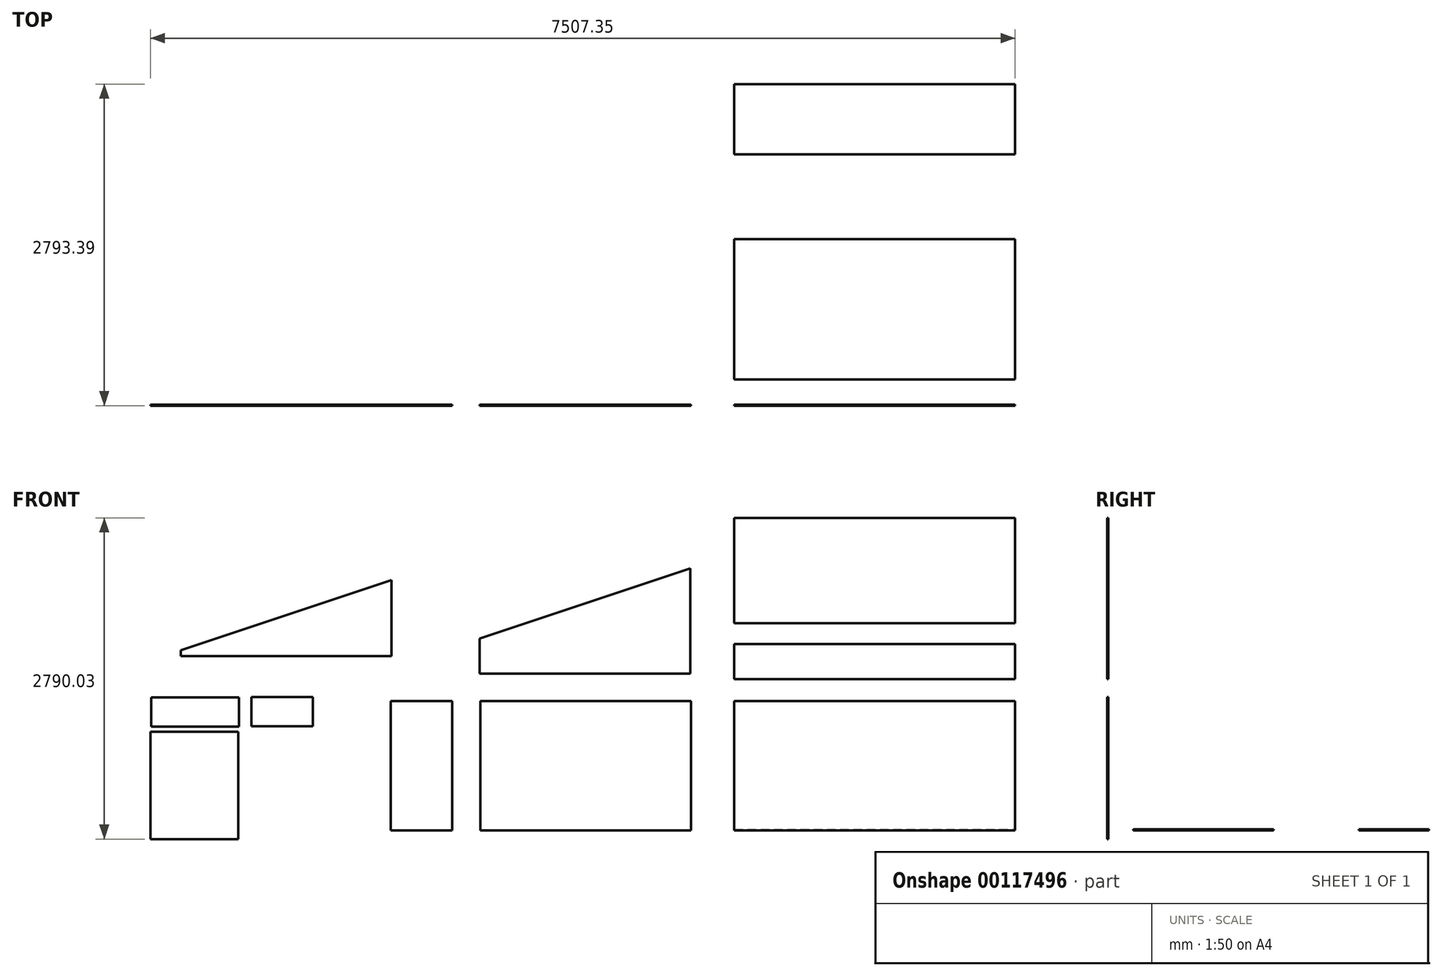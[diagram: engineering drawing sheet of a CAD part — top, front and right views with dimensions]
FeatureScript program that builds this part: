
annotation { "Feature Type Name" : "Feature", "Feature Type Description" : "" }
export const myFeature = defineFeature(function(context is Context, id is Id, definition is map)
    precondition{}
    {
        {
            var Q0;
            Q0=qCreatedBy(makeId("Front.planeOp"),FACE);
            var sketch = newSketch(context, id + "F0", { "sketchPlane" : qUnion([Q0])});
            skLineSegment(sketch, "E0.bottom", {"start": v(0, 0) * mm, "end": v(2438.4, 0) * mm});
            skLineSegment(sketch, "E0.top", {"start": v(0, 1123.95) * mm, "end": v(2438.4, 1123.95) * mm});
            skLineSegment(sketch, "E0.left", {"start": v(0, 0) * mm, "end": v(0, 1123.95) * mm});
            skLineSegment(sketch, "E0.right", {"start": v(2438.4, 0) * mm, "end": v(2438.4, 1123.95) * mm});
            skSolve(sketch);
        }
        {
            var Q0;
            Q0=makeQuery(id+"F0.imprint","IMPRINT",FACE,{"disambiguationData":[TD([[makeQuery(id+"F0.imprint","IMPRINT",EDGE,{"derivedFrom":sQuery(id+"F0.wireOp",EDGE,"E0.bottom")}),1.0]])]});
            extrude(context, id + "F1", {"entities" : qUnion([Q0]), "depth" : 9.52 * mm});
        }
        {
            var Q0;
            Q0=qCreatedBy(makeId("Front.planeOp"),FACE);
            var sketch = newSketch(context, id + "F2", { "sketchPlane" : qUnion([Q0])});
            skLineSegment(sketch, "E1.bottom", {"start": v(0, 1312.73) * mm, "end": v(2438.4, 1312.73) * mm});
            skLineSegment(sketch, "E1.top", {"start": v(0, 1617.53) * mm, "end": v(2438.4, 1617.53) * mm});
            skLineSegment(sketch, "E1.left", {"start": v(0, 1312.73) * mm, "end": v(0, 1617.53) * mm});
            skLineSegment(sketch, "E1.right", {"start": v(2438.4, 1312.73) * mm, "end": v(2438.4, 1617.53) * mm});
            skSolve(sketch);
        }
        {
            var Q0;
            Q0=makeQuery(id+"F2.imprint","IMPRINT",FACE,{"disambiguationData":[TD([[makeQuery(id+"F2.imprint","IMPRINT",EDGE,{"derivedFrom":sQuery(id+"F2.wireOp",EDGE,"E1.bottom")}),1.0]])]});
            extrude(context, id + "F3", {"entities" : qUnion([Q0]), "depth" : 9.52 * mm});
        }
        {
            var Q0;
            Q0=qCreatedBy(makeId("Front.planeOp"),FACE);
            var sketch = newSketch(context, id + "F4", { "sketchPlane" : qUnion([Q0])});
            skLineSegment(sketch, "E2.bottom", {"start": v(0, 1799.71) * mm, "end": v(2438.4, 1799.71) * mm});
            skLineSegment(sketch, "E2.top", {"start": v(0, 2714.11) * mm, "end": v(2438.4, 2714.11) * mm});
            skLineSegment(sketch, "E2.left", {"start": v(0, 1799.71) * mm, "end": v(0, 2714.11) * mm});
            skLineSegment(sketch, "E2.right", {"start": v(2438.4, 1799.71) * mm, "end": v(2438.4, 2714.11) * mm});
            skSolve(sketch);
        }
        {
            var Q0;
            Q0=makeQuery(id+"F4.imprint","IMPRINT",FACE,{"disambiguationData":[TD([[makeQuery(id+"F4.imprint","IMPRINT",EDGE,{"derivedFrom":sQuery(id+"F4.wireOp",EDGE,"E2.bottom")}),1.0]])]});
            extrude(context, id + "F5", {"entities" : qUnion([Q0]), "depth" : 9.52 * mm});
        }
        {
            var Q0;
            Q0=qCreatedBy(makeId("Front.planeOp"),FACE);
            var sketch = newSketch(context, id + "F6", { "sketchPlane" : qUnion([Q0])});
            skLineSegment(sketch, "E3.bottom", {"start": v(-374.82, 0) * mm, "end": v(-2203.62, 0) * mm});
            skLineSegment(sketch, "E3.top", {"start": v(-374.82, 1123.95) * mm, "end": v(-2203.62, 1123.95) * mm});
            skLineSegment(sketch, "E3.left", {"start": v(-374.82, 0) * mm, "end": v(-374.82, 1123.95) * mm});
            skLineSegment(sketch, "E3.right", {"start": v(-2203.62, 0) * mm, "end": v(-2203.62, 1123.95) * mm});
            skSolve(sketch);
        }
        {
            var Q0;
            Q0=makeQuery(id+"F6.imprint","IMPRINT",FACE,{"disambiguationData":[TD([[makeQuery(id+"F6.imprint","IMPRINT",EDGE,{"derivedFrom":sQuery(id+"F6.wireOp",EDGE,"E3.bottom")}),-1.0]])]});
            extrude(context, id + "F7", {"entities" : qUnion([Q0]), "depth" : 9.52 * mm});
        }
        {
            var Q0;
            Q0=qCreatedBy(makeId("Front.planeOp"),FACE);
            var sketch = newSketch(context, id + "F8", { "sketchPlane" : qUnion([Q0])});
            skLineSegment(sketch, "E4", {"start": v(-381.45, 1362.57) * mm, "end": v(-381.45, 2276.97) * mm});
            skLineSegment(sketch, "E5", {"start": v(-381.45, 2276.97) * mm, "end": v(-2210.25, 1667.37) * mm});
            skLineSegment(sketch, "E6", {"start": v(-2210.25, 1667.37) * mm, "end": v(-2210.25, 1362.57) * mm});
            skLineSegment(sketch, "E7", {"start": v(-2210.25, 1362.57) * mm, "end": v(-381.45, 1362.57) * mm});
            skSolve(sketch);
        }
        {
            var Q0;
            Q0=makeQuery(id+"F8.imprint","IMPRINT",FACE,{"disambiguationData":[TD([[makeQuery(id+"F8.imprint","IMPRINT",EDGE,{"derivedFrom":sQuery(id+"F8.wireOp",EDGE,"E4")}),1.0]])]});
            extrude(context, id + "F9", {"entities" : qUnion([Q0]), "depth" : 9.52 * mm});
        }
        {
            var Q0;
            Q0=qCreatedBy(makeId("Top.planeOp"),FACE);
            var sketch = newSketch(context, id + "F10", { "sketchPlane" : qUnion([Q0])});
            skLineSegment(sketch, "E8.bottom", {"start": v(0, 216.92) * mm, "end": v(2438.4, 216.92) * mm});
            skLineSegment(sketch, "E8.top", {"start": v(0, 1436.12) * mm, "end": v(2438.4, 1436.12) * mm});
            skLineSegment(sketch, "E8.left", {"start": v(0, 216.92) * mm, "end": v(0, 1436.12) * mm});
            skLineSegment(sketch, "E8.right", {"start": v(2438.4, 216.92) * mm, "end": v(2438.4, 1436.12) * mm});
            skSolve(sketch);
        }
        {
            var Q0;
            Q0=makeQuery(id+"F10.imprint","IMPRINT",FACE,{"disambiguationData":[TD([[makeQuery(id+"F10.imprint","IMPRINT",EDGE,{"derivedFrom":sQuery(id+"F10.wireOp",EDGE,"E8.bottom")}),1.0]])]});
            extrude(context, id + "F11", {"entities" : qUnion([Q0]), "depth" : 9.52 * mm});
        }
        {
            var Q0;
            Q0=qCreatedBy(makeId("Top.planeOp"),FACE);
            var sketch = newSketch(context, id + "F12", { "sketchPlane" : qUnion([Q0])});
            skLineSegment(sketch, "E9.bottom", {"start": v(0, 2174.26) * mm, "end": v(2438.4, 2174.26) * mm});
            skLineSegment(sketch, "E9.top", {"start": v(0, 2783.86) * mm, "end": v(2438.4, 2783.86) * mm});
            skLineSegment(sketch, "E9.left", {"start": v(0, 2174.26) * mm, "end": v(0, 2783.86) * mm});
            skLineSegment(sketch, "E9.right", {"start": v(2438.4, 2174.26) * mm, "end": v(2438.4, 2783.86) * mm});
            skSolve(sketch);
        }
        {
            var Q0;
            Q0=makeQuery(id+"F12.imprint","IMPRINT",FACE,{"disambiguationData":[TD([[makeQuery(id+"F12.imprint","IMPRINT",EDGE,{"derivedFrom":sQuery(id+"F12.wireOp",EDGE,"E9.bottom")}),1.0]])]});
            extrude(context, id + "F13", {"entities" : qUnion([Q0]), "depth" : 9.52 * mm});
        }
        {
            var Q0;
            Q0=qCreatedBy(makeId("Front.planeOp"),FACE);
            var sketch = newSketch(context, id + "F14", { "sketchPlane" : qUnion([Q0])});
            skLineSegment(sketch, "E10.bottom", {"start": v(-2447.4, 0) * mm, "end": v(-2980.8, 0) * mm});
            skLineSegment(sketch, "E10.top", {"start": v(-2447.4, 1123.95) * mm, "end": v(-2980.8, 1123.95) * mm});
            skLineSegment(sketch, "E10.left", {"start": v(-2447.4, 0) * mm, "end": v(-2447.4, 1123.95) * mm});
            skLineSegment(sketch, "E10.right", {"start": v(-2980.8, 0) * mm, "end": v(-2980.8, 1123.95) * mm});
            skSolve(sketch);
        }
        {
            var Q0;
            Q0=makeQuery(id+"F14.imprint","IMPRINT",FACE,{"disambiguationData":[TD([[makeQuery(id+"F14.imprint","IMPRINT",EDGE,{"derivedFrom":sQuery(id+"F14.wireOp",EDGE,"E10.bottom")}),-1.0]])]});
            extrude(context, id + "F15", {"entities" : qUnion([Q0]), "depth" : 9.52 * mm});
        }
        {
            var Q0;
            Q0=qCreatedBy(makeId("Front.planeOp"),FACE);
            var sketch = newSketch(context, id + "F16", { "sketchPlane" : qUnion([Q0])});
            skLineSegment(sketch, "E11", {"start": v(-2975.6, 1512.94) * mm, "end": v(-2975.6, 2173.34) * mm});
            skLineSegment(sketch, "E12", {"start": v(-2975.6, 2173.34) * mm, "end": v(-4804.4, 1563.74) * mm});
            skLineSegment(sketch, "E13", {"start": v(-4804.4, 1563.74) * mm, "end": v(-4804.4, 1512.94) * mm});
            skLineSegment(sketch, "E14", {"start": v(-4804.4, 1512.94) * mm, "end": v(-2975.6, 1512.94) * mm});
            skSolve(sketch);
        }
        {
            var Q0;
            Q0=makeQuery(id+"F16.imprint","IMPRINT",FACE,{"disambiguationData":[TD([[makeQuery(id+"F16.imprint","IMPRINT",EDGE,{"derivedFrom":sQuery(id+"F16.wireOp",EDGE,"E11")}),1.0]])]});
            extrude(context, id + "F17", {"entities" : qUnion([Q0]), "depth" : 9.52 * mm});
        }
        {
            var Q0;
            Q0=qCreatedBy(makeId("Front.planeOp"),FACE);
            var sketch = newSketch(context, id + "F18", { "sketchPlane" : qUnion([Q0])});
            skLineSegment(sketch, "E15.bottom", {"start": v(-3659.04, 1158.75) * mm, "end": v(-4192.44, 1158.75) * mm});
            skLineSegment(sketch, "E15.top", {"start": v(-3659.04, 904.75) * mm, "end": v(-4192.44, 904.75) * mm});
            skLineSegment(sketch, "E15.left", {"start": v(-3659.04, 1158.75) * mm, "end": v(-3659.04, 904.75) * mm});
            skLineSegment(sketch, "E15.right", {"start": v(-4192.44, 1158.75) * mm, "end": v(-4192.44, 904.75) * mm});
            skSolve(sketch);
        }
        {
            var Q0;
            Q0=makeQuery(id+"F18.imprint","IMPRINT",FACE,{"disambiguationData":[TD([[makeQuery(id+"F18.imprint","IMPRINT",EDGE,{"derivedFrom":sQuery(id+"F18.wireOp",EDGE,"E15.bottom")}),1.0]])]});
            extrude(context, id + "F19", {"entities" : qUnion([Q0]), "depth" : 9.52 * mm});
        }
        {
            var Q0;
            Q0=qCreatedBy(makeId("Front.planeOp"),FACE);
            var sketch = newSketch(context, id + "F20", { "sketchPlane" : qUnion([Q0])});
            skLineSegment(sketch, "E16.bottom", {"start": v(-4298.97, 901.37) * mm, "end": v(-5060.97, 901.37) * mm});
            skLineSegment(sketch, "E16.top", {"start": v(-4298.97, 1155.37) * mm, "end": v(-5060.97, 1155.37) * mm});
            skLineSegment(sketch, "E16.left", {"start": v(-4298.97, 901.37) * mm, "end": v(-4298.97, 1155.37) * mm});
            skLineSegment(sketch, "E16.right", {"start": v(-5060.97, 901.37) * mm, "end": v(-5060.97, 1155.37) * mm});
            skSolve(sketch);
        }
        {
            var Q0;
            Q0=makeQuery(id+"F20.imprint","IMPRINT",FACE,{"disambiguationData":[TD([[makeQuery(id+"F20.imprint","IMPRINT",EDGE,{"derivedFrom":sQuery(id+"F20.wireOp",EDGE,"E16.bottom")}),-1.0]])]});
            extrude(context, id + "F21", {"entities" : qUnion([Q0]), "depth" : 9.52 * mm});
        }
        {
            var Q0;
            Q0=qCreatedBy(makeId("Front.planeOp"),FACE);
            var sketch = newSketch(context, id + "F22", { "sketchPlane" : qUnion([Q0])});
            skLineSegment(sketch, "E17.bottom", {"start": v(-4306.95, 857.53) * mm, "end": v(-5068.95, 857.53) * mm});
            skLineSegment(sketch, "E17.top", {"start": v(-4306.95, -75.92) * mm, "end": v(-5068.95, -75.92) * mm});
            skLineSegment(sketch, "E17.left", {"start": v(-4306.95, 857.53) * mm, "end": v(-4306.95, -75.92) * mm});
            skLineSegment(sketch, "E17.right", {"start": v(-5068.95, 857.53) * mm, "end": v(-5068.95, -75.92) * mm});
            skSolve(sketch);
        }
        {
            var Q0;
            Q0=makeQuery(id+"F22.imprint","IMPRINT",FACE,{"disambiguationData":[TD([[makeQuery(id+"F22.imprint","IMPRINT",EDGE,{"derivedFrom":sQuery(id+"F22.wireOp",EDGE,"E17.bottom")}),1.0]])]});
            extrude(context, id + "F23", {"entities" : qUnion([Q0]), "depth" : 9.52 * mm});
        }
    });
